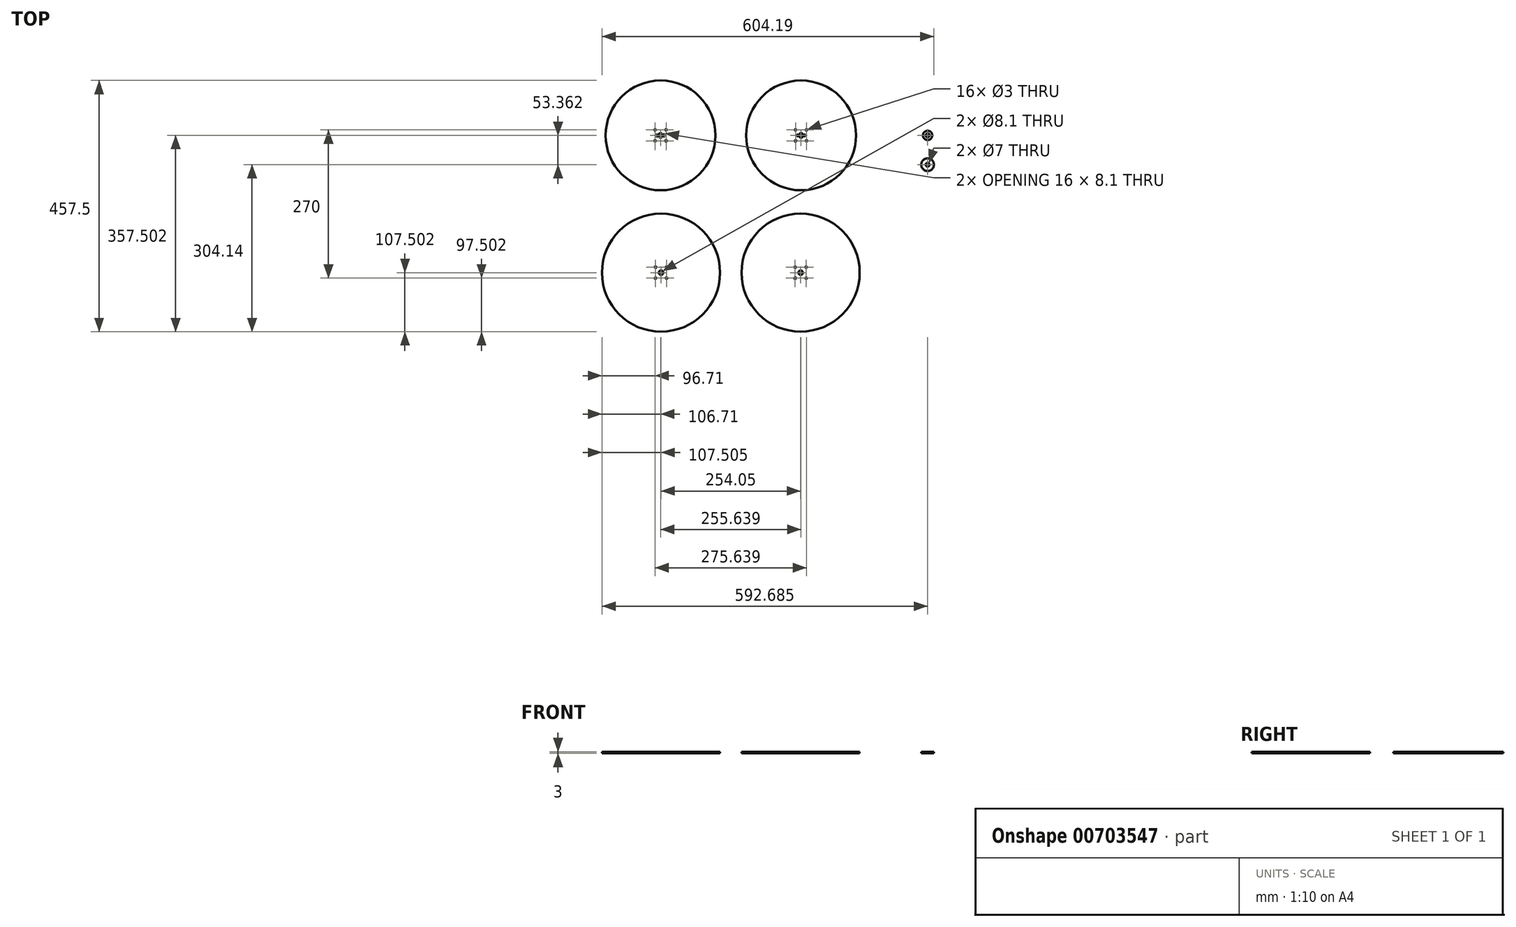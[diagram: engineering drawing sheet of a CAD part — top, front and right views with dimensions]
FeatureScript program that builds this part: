
annotation { "Feature Type Name" : "Feature", "Feature Type Description" : "" }
export const myFeature = defineFeature(function(context is Context, id is Id, definition is map)
    precondition{}
    {
        {
            var Q0;
            Q0=qCreatedBy(makeId("Top.planeOp"),FACE);
            var sketch = newSketch(context, id + "F0", { "sketchPlane" : qUnion([Q0])});
            skCircle(sketch, "E0", {"center": v(-127.82, 53.36) * mm, "radius": 100 * mm});
            skCircle(sketch, "E1", {"center": v(-127.03, -196.64) * mm, "radius": 107.5 * mm});
            skLineSegment(sketch, "E2.bottom", {"start": v(-117.82, 63.36) * mm, "end": v(-137.82, 63.36) * mm, "construction": true});
            skLineSegment(sketch, "E2.top", {"start": v(-117.82, 43.36) * mm, "end": v(-137.82, 43.36) * mm, "construction": true});
            skLineSegment(sketch, "E2.left", {"start": v(-117.82, 63.36) * mm, "end": v(-117.82, 43.36) * mm, "construction": true});
            skLineSegment(sketch, "E2.right", {"start": v(-137.82, 63.36) * mm, "end": v(-137.82, 43.36) * mm, "construction": true});
            skLineSegment(sketch, "E3.bottom", {"start": v(-117.03, -186.64) * mm, "end": v(-137.03, -186.64) * mm, "construction": true});
            skLineSegment(sketch, "E3.top", {"start": v(-117.03, -206.64) * mm, "end": v(-137.03, -206.64) * mm, "construction": true});
            skLineSegment(sketch, "E3.left", {"start": v(-117.03, -186.64) * mm, "end": v(-117.03, -206.64) * mm, "construction": true});
            skLineSegment(sketch, "E3.right", {"start": v(-137.03, -186.64) * mm, "end": v(-137.03, -206.64) * mm, "construction": true});
            skCircle(sketch, "E4", {"center": v(-127.82, 53.36) * mm, "radius": 4.05 * mm});
            skCircle(sketch, "E5", {"center": v(-127.03, -196.64) * mm, "radius": 4.05 * mm});
            skCircle(sketch, "E6", {"center": v(-137.82, 63.36) * mm, "radius": 1.5 * mm});
            skCircle(sketch, "E7", {"center": v(-117.82, 63.36) * mm, "radius": 1.5 * mm});
            skCircle(sketch, "E8", {"center": v(-117.82, 43.36) * mm, "radius": 1.5 * mm});
            skCircle(sketch, "E9", {"center": v(-137.82, 43.36) * mm, "radius": 1.5 * mm});
            skCircle(sketch, "E10", {"center": v(-137.03, -186.64) * mm, "radius": 1.5 * mm});
            skCircle(sketch, "E11", {"center": v(-137.03, -206.64) * mm, "radius": 1.5 * mm});
            skCircle(sketch, "E12", {"center": v(-117.03, -206.64) * mm, "radius": 1.5 * mm});
            skCircle(sketch, "E13", {"center": v(-117.03, -186.64) * mm, "radius": 1.5 * mm});
            skCircle(sketch, "E14.MirrorC", {"center": v(127.02, -196.64) * mm, "radius": 107.5 * mm});
            skCircle(sketch, "E15.MirrorC", {"center": v(127.82, 53.36) * mm, "radius": 100 * mm});
            skLineSegment(sketch, "E16.bottom", {"start": v(-119.82, 51.86) * mm, "end": v(-135.82, 51.86) * mm});
            skLineSegment(sketch, "E16.top", {"start": v(-119.82, 54.86) * mm, "end": v(-135.82, 54.86) * mm});
            skLineSegment(sketch, "E16.left", {"start": v(-119.82, 51.86) * mm, "end": v(-119.82, 54.86) * mm});
            skLineSegment(sketch, "E16.right", {"start": v(-135.82, 51.86) * mm, "end": v(-135.82, 54.86) * mm});
            skCircle(sketch, "E17", {"center": v(358.16, 53.36) * mm, "radius": 8.5 * mm});
            skCircle(sketch, "E18", {"center": v(358.16, 53.36) * mm, "radius": 3.5 * mm});
            skLineSegment(sketch, "E19", {"start": v(400.21, 98.02) * mm, "end": v(400.21, -116.57) * mm, "construction": true});
            skCircle(sketch, "E20.MirrorC", {"center": v(442.27, 53.36) * mm, "radius": 8.5 * mm});
            skCircle(sketch, "E21.MirrorC", {"center": v(442.27, 53.36) * mm, "radius": 3.5 * mm});
            skCircle(sketch, "E22", {"center": v(358.16, 0) * mm, "radius": 11.5 * mm});
            skCircle(sketch, "E23", {"center": v(358.16, 0) * mm, "radius": 3.5 * mm});
            skCircle(sketch, "E24.MirrorC", {"center": v(442.27, 0) * mm, "radius": 11.5 * mm});
            skCircle(sketch, "E25.MirrorC", {"center": v(442.27, 0) * mm, "radius": 3.5 * mm});
            skSolve(sketch);
        }
        {
            var Q0;
            Q0=makeQuery(id+"F0.imprint","IMPRINT",FACE,{"disambiguationData":[TD([[makeQuery(id+"F0.imprint","IMPRINT",EDGE,{"derivedFrom":sQuery(id+"F0.wireOp",EDGE,"E0")}),1.0]])]});
            var Q1;
            Q1=makeQuery(id+"F0.imprint","IMPRINT",FACE,{"disambiguationData":[TD([[makeQuery(id+"F0.imprint","IMPRINT",EDGE,{"derivedFrom":sQuery(id+"F0.wireOp",EDGE,"E1")}),1.0]])]});
            var Q2;
            Q2=makeQuery(id+"F0.imprint","IMPRINT",FACE,{"disambiguationData":[TD([[makeQuery(id+"F0.imprint","IMPRINT",EDGE,{"derivedFrom":sQuery(id+"F0.wireOp",EDGE,"E17")}),1.0]])]});
            var Q3;
            Q3=makeQuery(id+"F0.imprint","IMPRINT",FACE,{"disambiguationData":[TD([[makeQuery(id+"F0.imprint","IMPRINT",EDGE,{"derivedFrom":sQuery(id+"F0.wireOp",EDGE,"E20.MirrorC")}),-1.0]])]});
            var Q4;
            Q4=makeQuery(id+"F0.imprint","IMPRINT",FACE,{"disambiguationData":[TD([[makeQuery(id+"F0.imprint","IMPRINT",EDGE,{"derivedFrom":sQuery(id+"F0.wireOp",EDGE,"E22")}),1.0]])]});
            var Q5;
            Q5=makeQuery(id+"F0.imprint","IMPRINT",FACE,{"disambiguationData":[TD([[makeQuery(id+"F0.imprint","IMPRINT",EDGE,{"derivedFrom":sQuery(id+"F0.wireOp",EDGE,"E24.MirrorC")}),-1.0]])]});
            extrude(context, id + "F1", {"entities" : qUnion([Q0, Q1, Q2, Q3, Q4, Q5]), "depth" : 3 * mm, "offsetDistance" : 25 * mm});
        }
        {
            var Q0;
            Q0=makeQuery(id+"F1.opExtrude","SWEPT_BODY",BODY,{"disambiguationData":[OSD([sQuery(id+"F0.wireOp",EDGE,"E0"),sQuery(id+"F0.wireOp",EDGE,"E4"),sQuery(id+"F0.wireOp",EDGE,"E6"),sQuery(id+"F0.wireOp",EDGE,"E7"),sQuery(id+"F0.wireOp",EDGE,"E8"),sQuery(id+"F0.wireOp",EDGE,"E9")])]});
            var Q1;
            Q1=makeQuery(id+"F1.opExtrude","SWEPT_BODY",BODY,{"disambiguationData":[OSD([sQuery(id+"F0.wireOp",EDGE,"E1"),sQuery(id+"F0.wireOp",EDGE,"E5"),sQuery(id+"F0.wireOp",EDGE,"E10"),sQuery(id+"F0.wireOp",EDGE,"E11"),sQuery(id+"F0.wireOp",EDGE,"E12"),sQuery(id+"F0.wireOp",EDGE,"E13")])]});
            var Q2;
            Q2=qCreatedBy(makeId("Right.planeOp"),FACE);
            mirror(context, id + "F2", {"entities" : qUnion([Q0, Q1]), "mirrorPlane" : qUnion([Q2])});
        }
    });
